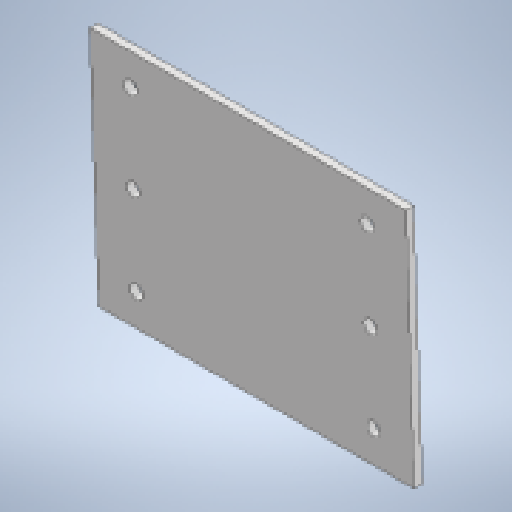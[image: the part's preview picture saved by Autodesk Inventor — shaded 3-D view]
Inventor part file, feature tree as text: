
AUTODESK INVENTOR PART (.ipt)
format: ipt  version: 2025 (Build 290162010, 162A)  size: 237,568 bytes
history: native  units: mm
features: sheet_metal_op x1, sketch x1, other x1
ambient origin geometry x8: Origin, YZ Plane, XZ Plane, XY Plane, X Axis, Y Axis, Z Axis, Center Point
bodies: Body1 (feature_tree)
feature tree (3):
  sheet_metal_op  "Face2"
  sketch  "Sketch5"  dims[d26=400.0mm d27=0.349066mm d28=400.0mm d29=300.0mm d30=10.0mm d31=50.0mm d33=40.0mm d34=40.0mm d35=17.0mm]
  other  "Plate3"
